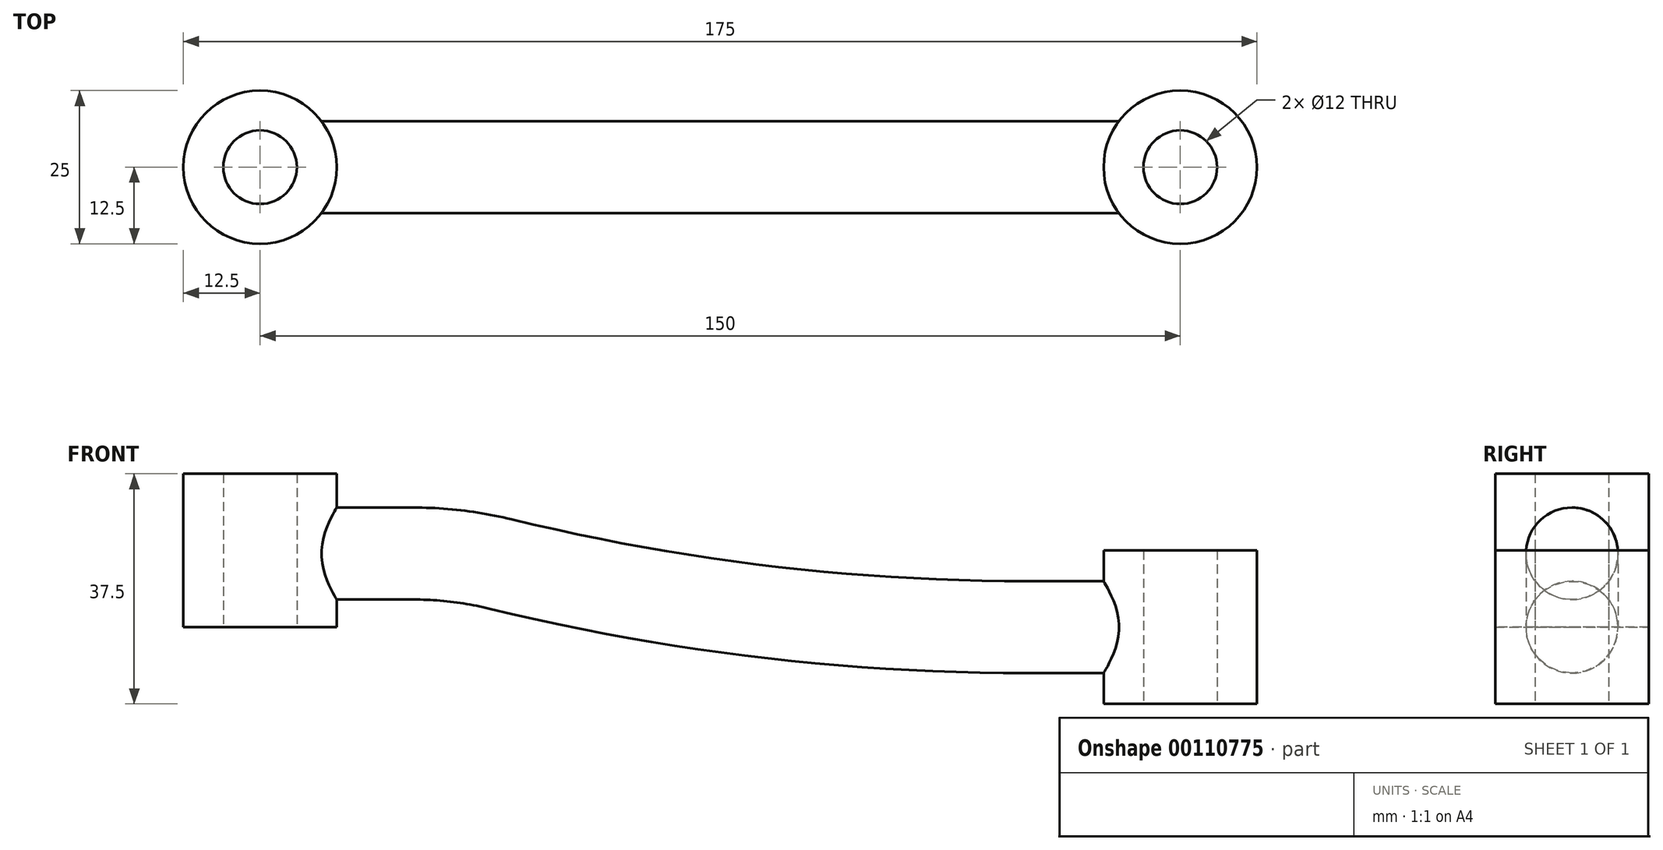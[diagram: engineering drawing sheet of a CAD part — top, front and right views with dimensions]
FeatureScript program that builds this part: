
annotation { "Feature Type Name" : "Feature", "Feature Type Description" : "" }
export const myFeature = defineFeature(function(context is Context, id is Id, definition is map)
    precondition{}
    {
        {
            var Q0;
            Q0=qCreatedBy(makeId("Top.planeOp"),FACE);
            var sketch = newSketch(context, id + "F0", { "sketchPlane" : qUnion([Q0])});
            skCircle(sketch, "E0", {"center": v(0, 0) * mm, "radius": 12.5 * mm});
            skCircle(sketch, "E1", {"center": v(0, 0) * mm, "radius": 6 * mm});
            skSolve(sketch);
        }
        {
            var Q0;
            Q0=makeQuery(id+"F0.imprint","IMPRINT",FACE,{"disambiguationData":[TD([[makeQuery(id+"F0.imprint","IMPRINT",EDGE,{"derivedFrom":sQuery(id+"F0.wireOp",EDGE,"E0")}),1.0]])]});
            extrude(context, id + "F1", {"entities" : qUnion([Q0]), "depth" : 25 * mm});
        }
        {
            var Q0;
            Q0=qCreatedBy(makeId("Front.planeOp"),FACE);
            var sketch = newSketch(context, id + "F2", { "sketchPlane" : qUnion([Q0])});
            skLineSegment(sketch, "E2", {"start": v(0, 12) * mm, "end": v(25, 12) * mm});
            skArc(sketch, "E3", {"start": v(39.2, 10.3) * mm, "mid": v(81.79, 2.58) * mm, "end": v(125, 0) * mm});
            skLineSegment(sketch, "E4", {"start": v(125, 0) * mm, "end": v(150, 0) * mm});
            skArc(sketch, "E5.filletArc", {"start": v(39.2, 10.3) * mm, "mid": v(32.15, 11.57) * mm, "end": v(25, 12) * mm});
            skSolve(sketch);
        }
        {
            var Q0;
            Q0=qCreatedBy(makeId("Right.planeOp"),FACE);
            var sketch = newSketch(context, id + "F3", { "sketchPlane" : qUnion([Q0])});
            skCircle(sketch, "E6", {"center": v(0, 12) * mm, "radius": 7.5 * mm});
            skSolve(sketch);
        }
        {
            var Q0;
            Q0=qCreatedBy(makeId("Top.planeOp"),FACE);
            var sketch = newSketch(context, id + "F4", { "sketchPlane" : qUnion([Q0])});
            skCircle(sketch, "E7", {"center": v(150, 0) * mm, "radius": 12.5 * mm});
            skCircle(sketch, "E8", {"center": v(150, 0) * mm, "radius": 6 * mm});
            skSolve(sketch);
        }
        {
            var Q0;
            Q0 = qSketchRegion(id + "F3", true);
            var Q1;
            Q1=sQuery(id+"F2.wireOp",EDGE,"E2");
            var Q2;
            Q2=sQuery(id+"F2.wireOp",EDGE,"E5.filletArc");
            var Q3;
            Q3=sQuery(id+"F2.wireOp",EDGE,"E3");
            var Q4;
            Q4=sQuery(id+"F2.wireOp",EDGE,"E4");
            sweep(context, id + "F5", {"operationType" : NewBodyOperationType.ADD, "profiles" : qUnion([Q0]), "path" : qUnion([Q1, Q2, Q3, Q4])});
        }
        {
            var Q0;
            Q0=makeQuery(id+"F4.imprint","IMPRINT",FACE,{"disambiguationData":[TD([[makeQuery(id+"F4.imprint","IMPRINT",EDGE,{"derivedFrom":sQuery(id+"F4.wireOp",EDGE,"E7")}),1.0]])]});
            extrude(context, id + "F6", {"entities" : qUnion([Q0]), "operationType" : NewBodyOperationType.ADD, "endBound" : BoundingType.SYMMETRIC, "depth" : 25 * mm});
        }
        {
            var Q0;
            Q0=qCreatedBy(makeId("Top.planeOp"),FACE);
            var sketch = newSketch(context, id + "F7", { "sketchPlane" : qUnion([Q0])});
            skCircle(sketch, "E9", {"center": v(0, 0) * mm, "radius": 6 * mm});
            skSolve(sketch);
        }
        {
            var Q0;
            Q0 = qSketchRegion(id + "F7", true);
            extrude(context, id + "F8", {"entities" : qUnion([Q0]), "operationType" : NewBodyOperationType.REMOVE, "endBound" : BoundingType.THROUGH_ALL, "depth" : 25 * mm});
        }
        {
            var Q0;
            Q0=makeQuery(id+"F4.imprint","IMPRINT",FACE,{"disambiguationData":[TD([[makeQuery(id+"F4.imprint","IMPRINT",EDGE,{"derivedFrom":sQuery(id+"F4.wireOp",EDGE,"E8")}),1.0]])]});
            extrude(context, id + "F9", {"entities" : qUnion([Q0]), "operationType" : NewBodyOperationType.REMOVE, "endBound" : BoundingType.SYMMETRIC, "depth" : 25 * mm});
        }
    });
